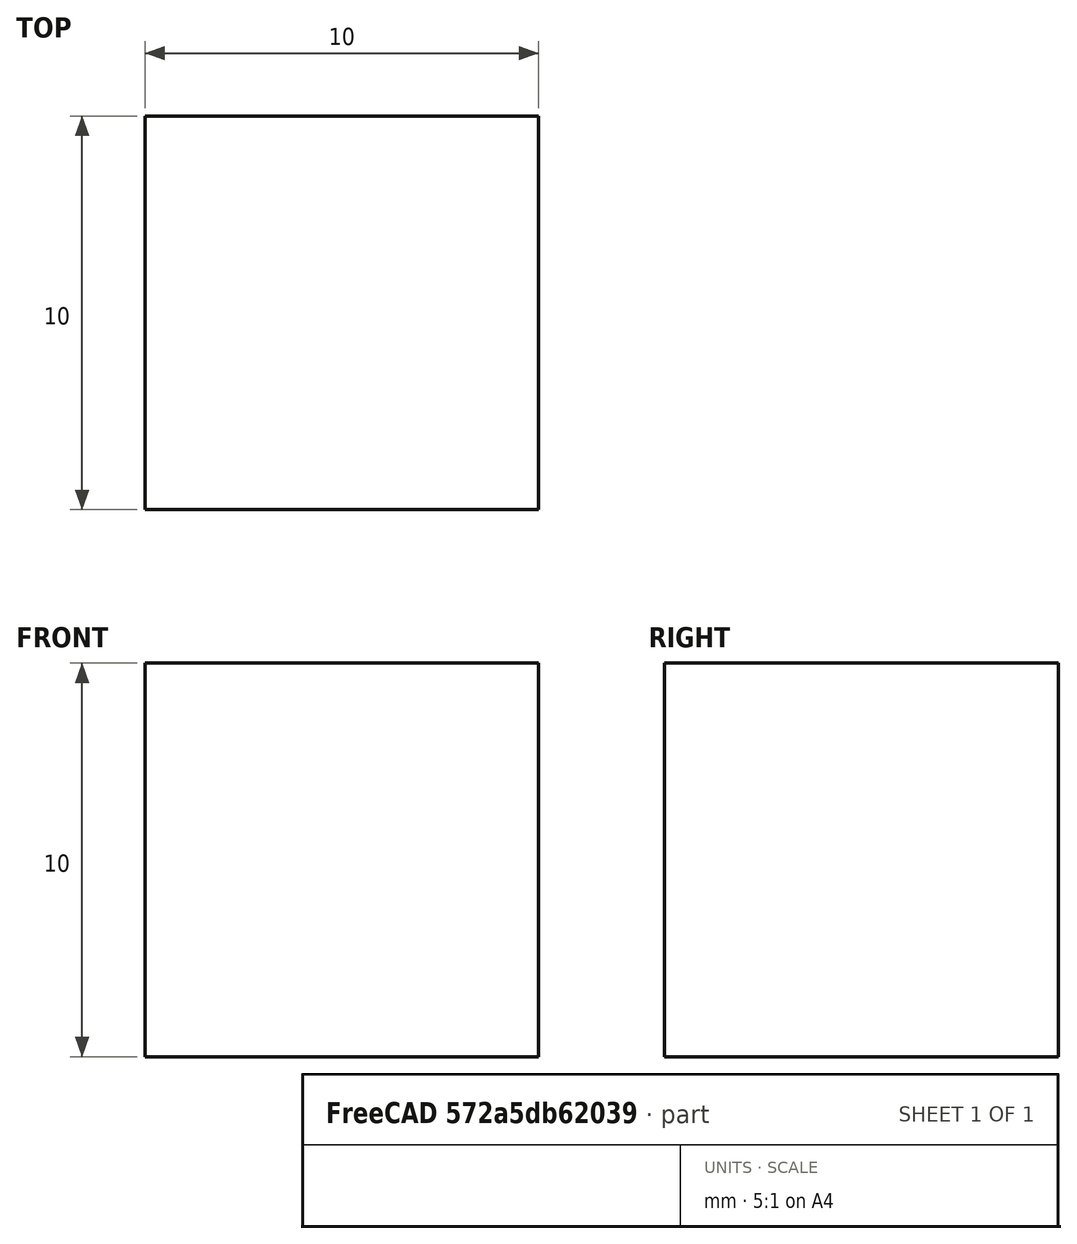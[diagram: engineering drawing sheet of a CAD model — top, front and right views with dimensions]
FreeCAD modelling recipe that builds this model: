
FCSTD DOCUMENT  (FreeCAD 0.21R33694 (Git))
Label: RR_test
License: All rights reserved
LicenseURL: http://en.wikipedia.org/wiki/All_rights_reserved
objects: Fem::ConstraintDisplacement×3, Part::Box×1, Fem::ConstraintPressure×1, Fem::FemAnalysis×1
note: 1 computed .brp shape members not serialized (recipe doc carries the construction recipe); baked Part::Feature solids carry a one-line shape summary decoded from their .brp

FEATURE [Part::Box] Box  label="Cube"
  AttacherType = Attacher::AttachEngine3D
  Height = 10
  Length = 10
  Width = 10
FEATURE [Fem::ConstraintPressure] ConstraintPressure
  NormalDirection = (0,0,1)
  Normals = (9) [(0,0,1),(0,0,1),(0,0,1),(0,0,1),(0,0,1),(0,0,1),(0,0,1),(0,0,1),(0,0,1)]
  Points = (9) [(0,0,10),(5,0,10),(10,0,10),(0,5,10),(5,5,10),(10,5,10),(0,10,10),(5,10,10),(10,10,10)]
  Pressure = 1
  References = -> [Box]
  Reversed = true
FEATURE [Fem::ConstraintDisplacement] ConstraintDisplacement
  NormalDirection = (0,0,-1)
  Normals = (9) [(0,0,-1),(0,0,-1),(0,0,-1),(0,0,-1),(0,0,-1),(0,0,-1),(0,0,-1),(0,0,-1),(0,0,-1)]
  Points = (9) [(0,0,0),(5,0,0),(10,0,0),(0,5,0),(5,5,0),(10,5,0),(0,10,0),(5,10,0),(10,10,0)]
  References = -> [Box]
  hasXFormula = false
  hasYFormula = false
  hasZFormula = false
  rotxFix = false
  rotxFree = true
  rotyFix = false
  rotyFree = true
  rotzFix = false
  rotzFree = true
  useFlowSurfaceForce = false
  xDisplacement = 0
  xFix = false
  xFree = true
  xRotation = 0
  yDisplacement = 0
  yFix = false
  yFree = true
  yRotation = 0
  zDisplacement = 0
  zFix = false
  zFree = false
  zRotation = 0
FEATURE [Fem::ConstraintDisplacement] ConstraintDisplacement001
  NormalDirection = (0,0,1)
  Normals = (1) [(0,0,1)]
  Points = (1) [(0,0,0)]
  References = -> [Box]
  Scale = 2
  hasXFormula = false
  hasYFormula = false
  hasZFormula = false
  rotxFix = false
  rotxFree = true
  rotyFix = false
  rotyFree = true
  rotzFix = false
  rotzFree = true
  useFlowSurfaceForce = false
  xDisplacement = 0
  xFix = false
  xFree = false
  xRotation = 0
  yDisplacement = 0
  yFix = false
  yFree = false
  yRotation = 0
  zDisplacement = 0
  zFix = false
  zFree = true
  zRotation = 0
FEATURE [Fem::ConstraintDisplacement] ConstraintDisplacement002
  NormalDirection = (0,0,1)
  Normals = (1) [(0,0,1)]
  Points = (1) [(10,0,0)]
  References = -> [Box]
  Scale = 2
  hasXFormula = false
  hasYFormula = false
  hasZFormula = false
  rotxFix = false
  rotxFree = true
  rotyFix = false
  rotyFree = true
  rotzFix = false
  rotzFree = true
  useFlowSurfaceForce = false
  xDisplacement = 0
  xFix = false
  xFree = true
  xRotation = 0
  yDisplacement = 0
  yFix = false
  yFree = false
  yRotation = 0
  zDisplacement = 0
  zFix = false
  zFree = true
  zRotation = 0
FEATURE [Fem::FemAnalysis] Analysis
  Group = -> [ConstraintPressure,ConstraintDisplacement,ConstraintDisplacement001,ConstraintDisplacement002]
